# Revit family: Thorn HiPak GEN4 M
name_source: partatom
category: Lighting Fixtures
revit_build: Autodesk Revit 2018 (Build: 20170223_1515(x64)
units: mm (PartAtom-declared; Revit-internal decimal feet)

## family parameters
Cut with Voids When Loaded = No
Host = Face
Light Source = Yes
OmniClass Number = 23.80.70.11
OmniClass Title = Luminaries for Internal Lighting
Part Type = Normal
Room Calculation Point = No
Round Connector Dimension = Use Diameter
Shared = No

## types (1)
- HIPAK G4 M LED25000-840 WB HF QC5
    Apparent Load = 148 VA
    Assembly Code = D5020200
    Color Filter = 16777215
    Default Elevation = 0 mm  [stored 0 ft]
    Description = LED industrial luminaire
    Dimming Lamp Color Temperature Shift = <None>
    Emit Shape Visible in Rendering = No
    Emit from Circle Diameter = 294 mm  [stored 0.964567 ft]
    Height = 170 mm
    Lamp = LED
    Length = 320 mm
    Manufacturer = Thorn Lighting
    Model = 96636209
    Photometric Web File = 96636209_(STD).IES
    Tilt Angle = -90.00°
    URL = www.thornlighting.com/96636209
    Voltage = 230 V
    Width = 320 mm

note: [stored X ft] marks values corroborated as IEEE doubles in the binary element streams (Revit-internal decimal feet)

## geometry (parser evidence)
native form markers: Sweep x5
no freeform markers — native parametric forms only
